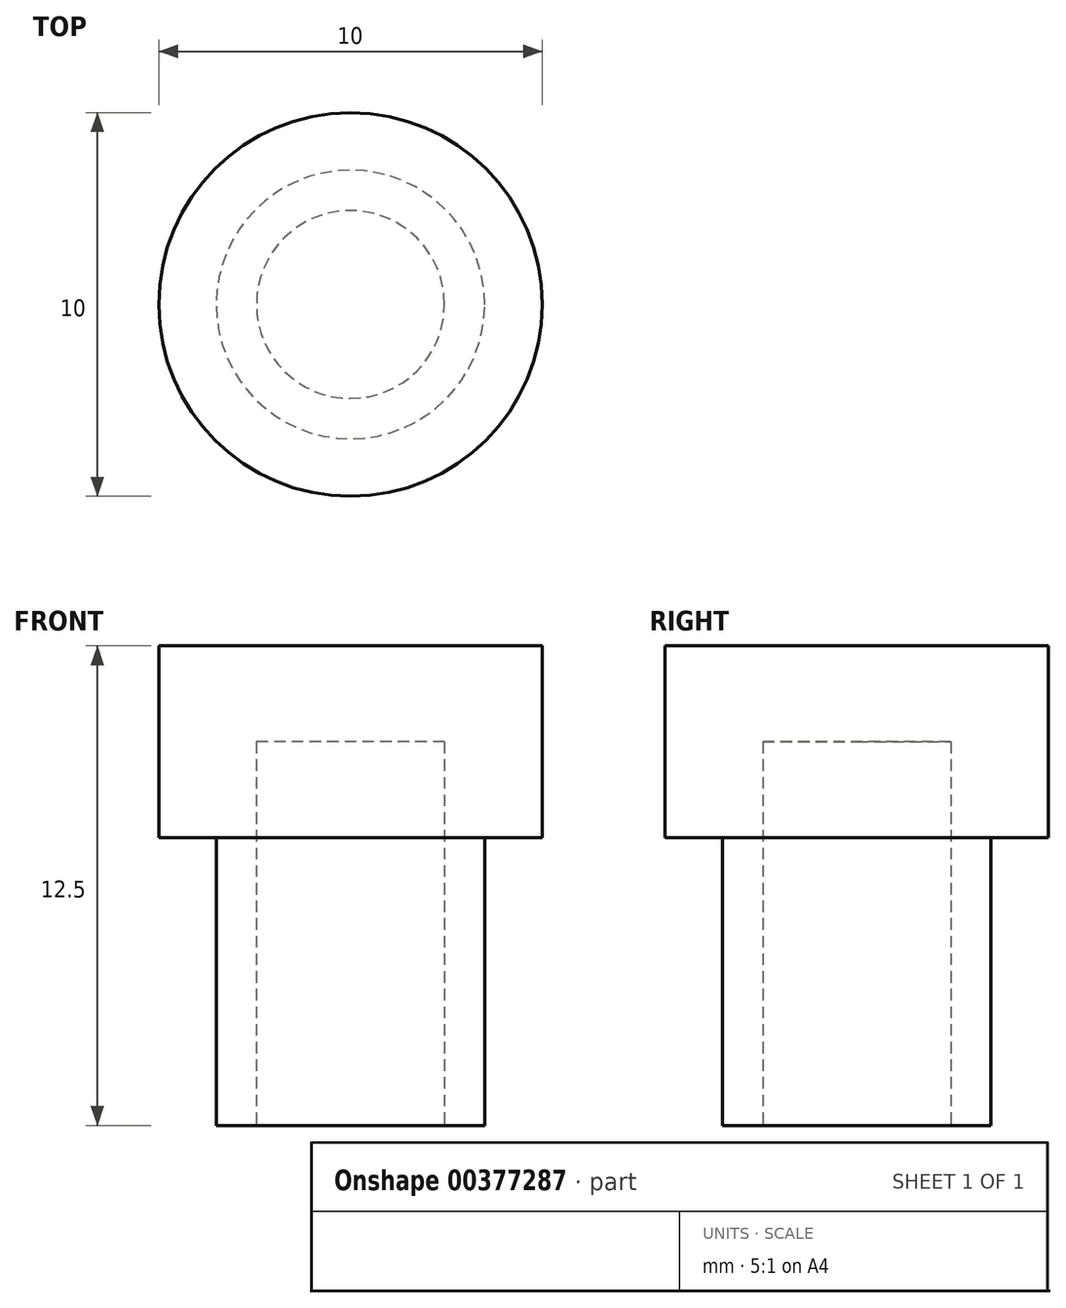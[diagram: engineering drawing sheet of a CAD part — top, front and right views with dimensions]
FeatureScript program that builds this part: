
annotation { "Feature Type Name" : "Feature", "Feature Type Description" : "" }
export const myFeature = defineFeature(function(context is Context, id is Id, definition is map)
    precondition{}
    {
        {
            var Q0;
            Q0=qCreatedBy(makeId("Top.planeOp"),FACE);
            var sketch = newSketch(context, id + "F0", { "sketchPlane" : qUnion([Q0])});
            skCircle(sketch, "E0", {"center": v(0, 0) * mm, "radius": 3.5 * mm});
            skCircle(sketch, "E1", {"center": v(0, 0) * mm, "radius": 2.45 * mm});
            skSolve(sketch);
        }
        {
            var Q0;
            Q0 = qSketchRegion(id + "F0", true);
            extrude(context, id + "F1", {"entities" : qUnion([Q0]), "depth" : 7.5 * mm});
        }
        {
            var Q0;
            Q0=makeQuery(id+"F1.opExtrude","CAP_FACE",FACE,{"disambiguationData":[OSD([sQuery(id+"F0.wireOp",EDGE,"E0"),sQuery(id+"F0.wireOp",EDGE,"E1")])],"isStart":false});
            var sketch = newSketch(context, id + "F2", { "sketchPlane" : qUnion([Q0])});
            skCircle(sketch, "E2", {"center": v(0, 0) * mm, "radius": 5 * mm});
            skSolve(sketch);
        }
        {
            var Q0;
            Q0 = qSketchRegion(id + "F2", true);
            extrude(context, id + "F3", {"entities" : qUnion([Q0]), "operationType" : NewBodyOperationType.ADD, "depth" : 5 * mm});
        }
        {
            var Q0;
            Q0=makeQuery(id+"F3.boolean.opBoolean","SPLIT",FACE,{"disambiguationData":[TD([makeQuery(id+"F1.opExtrude","SWEPT_FACE",FACE,{"disambiguationData":[OSD([sQuery(id+"F0.wireOp",EDGE,"E1")])]})])],"derivedFrom":makeQuery(id+"F3.opExtrude","CAP_FACE",FACE,{"disambiguationData":[OSD([sQuery(id+"F2.wireOp",EDGE,"E2")])],"isStart":true})});
            var sketch = newSketch(context, id + "F4", { "sketchPlane" : qUnion([Q0])});
            skCircle(sketch, "E3", {"center": v(0, 0) * mm, "radius": 2.45 * mm});
            skSolve(sketch);
        }
        {
            var Q0;
            Q0 = qSketchRegion(id + "F4", true);
            extrude(context, id + "F5", {"entities" : qUnion([Q0]), "operationType" : NewBodyOperationType.REMOVE, "oppositeDirection" : true, "depth" : 2.5 * mm});
        }
    });
